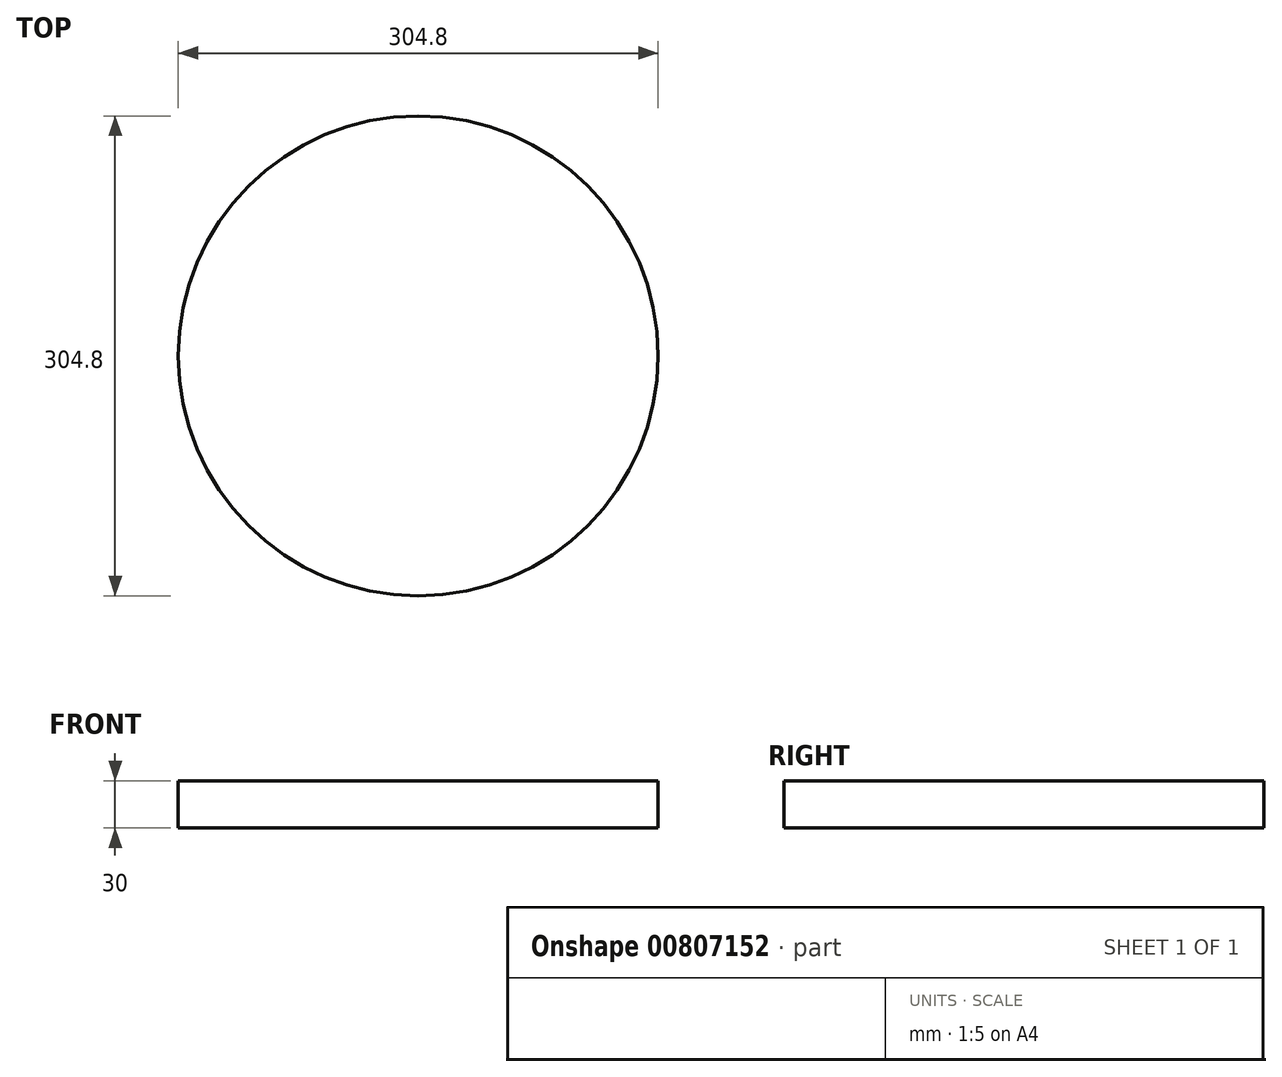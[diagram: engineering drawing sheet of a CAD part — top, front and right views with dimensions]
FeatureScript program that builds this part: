
annotation { "Feature Type Name" : "Feature", "Feature Type Description" : "" }
export const myFeature = defineFeature(function(context is Context, id is Id, definition is map)
    precondition{}
    {
        {
            var Q0;
            Q0=qCreatedBy(makeId("Top.planeOp"),FACE);
            var sketch = newSketch(context, id + "F0", { "sketchPlane" : qUnion([Q0])});
            skCircle(sketch, "E0", {"center": v(0, 0) * mm, "radius": 152.4 * mm});
            skSolve(sketch);
        }
        {
            var Q0;
            Q0=qSketchRegion(id+"F0",true);
            extrude(context, id + "F1", {"entities" : qUnion([Q0]), "depth" : 30 * mm, "offsetDistance" : 25.4 * mm});
        }
    });
